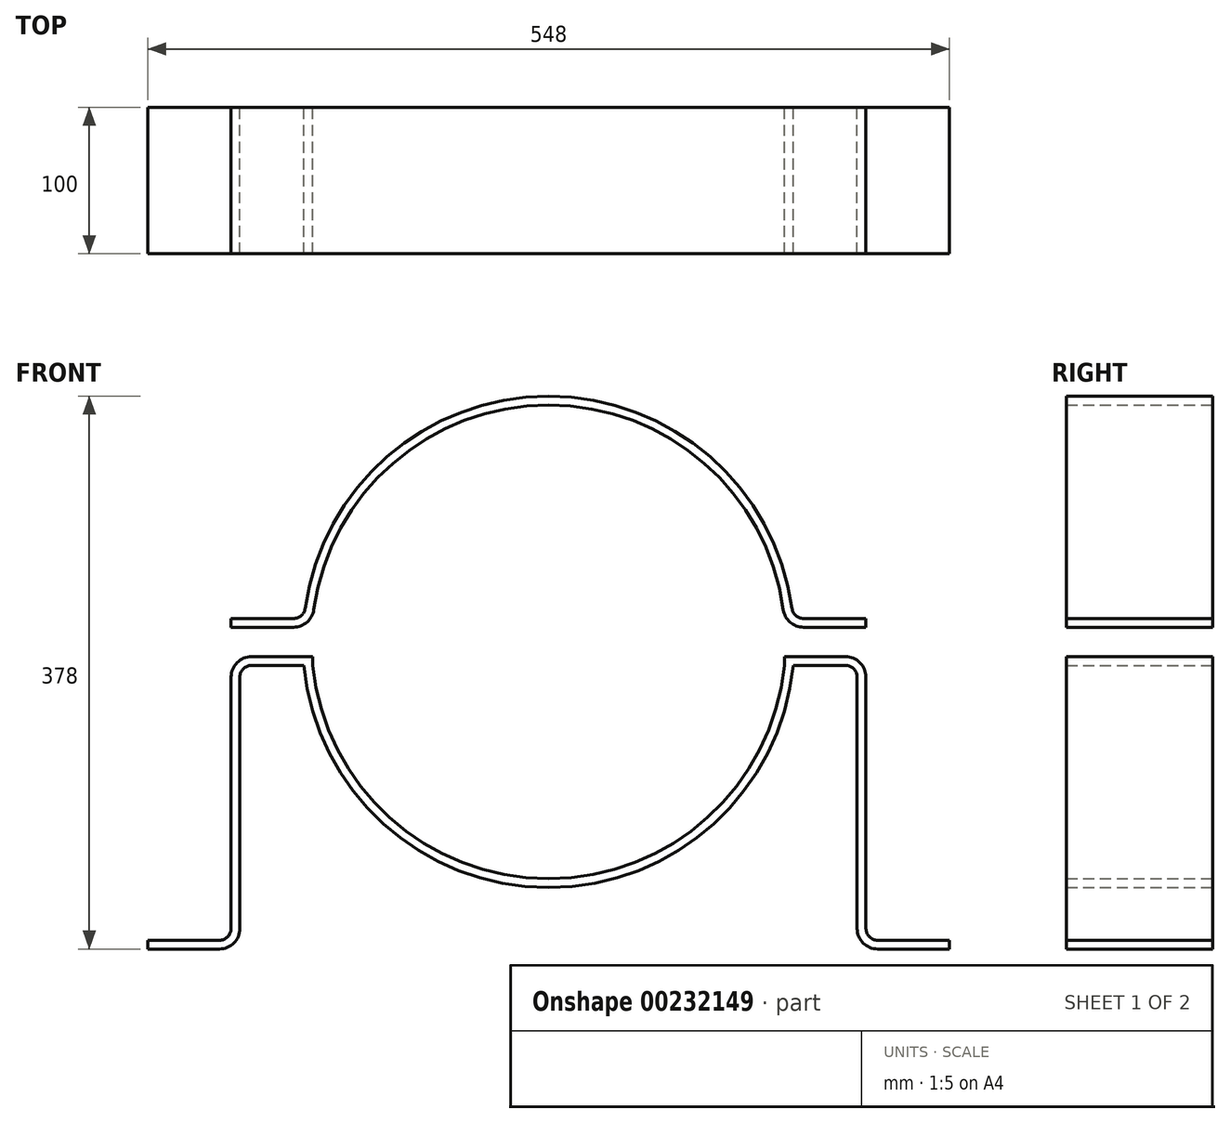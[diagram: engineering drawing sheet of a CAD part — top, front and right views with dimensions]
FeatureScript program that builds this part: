
annotation { "Feature Type Name" : "Feature", "Feature Type Description" : "" }
export const myFeature = defineFeature(function(context is Context, id is Id, definition is map)
    precondition{}
    {
        {
            var Q0;
            Q0=qCreatedBy(makeId("Front.planeOp"),FACE);
            var sketch = newSketch(context, id + "F0", { "sketchPlane" : qUnion([Q0])});
            skArc(sketch, "E0", {"start": v(160.49, 22.1) * mm, "mid": v(0, 162) * mm, "end": v(-160.49, 22.1) * mm});
            skArc(sketch, "E1.0", {"start": v(166.43, 22.9) * mm, "mid": v(0, 168) * mm, "end": v(-166.43, 22.9) * mm});
            skLineSegment(sketch, "E2", {"start": v(-168, 0) * mm, "end": v(168, 0) * mm, "construction": true});
            skLineSegment(sketch, "E3.0", {"start": v(-203, -10) * mm, "end": v(-161.2, -10) * mm});
            skLineSegment(sketch, "E4.0", {"start": v(-217, 10) * mm, "end": v(-174.36, 10) * mm});
            skLineSegment(sketch, "E5.0", {"start": v(-217, 16) * mm, "end": v(-174.36, 16) * mm});
            skLineSegment(sketch, "E6.0", {"start": v(-203, -16) * mm, "end": v(-161.2, -16) * mm});
            skLineSegment(sketch, "E7", {"start": v(0, 0) * mm, "end": v(0, -223.8) * mm, "construction": true});
            skLineSegment(sketch, "E8.0", {"start": v(-217, 16) * mm, "end": v(-217, 10) * mm});
            skLineSegment(sketch, "E9.0", {"start": v(217, 16) * mm, "end": v(217, 10) * mm});
            skPoint(sketch, "E10.orphan", {"position": v(-259.53, 0) * mm});
            skLineSegment(sketch, "E11.trimOffspring", {"start": v(-217, -24) * mm, "end": v(-217, -196) * mm});
            skLineSegment(sketch, "E12.trimOffspring", {"start": v(217, -24) * mm, "end": v(217, -196) * mm});
            skLineSegment(sketch, "E13", {"start": v(-225, -210) * mm, "end": v(-274, -210) * mm});
            skLineSegment(sketch, "E14", {"start": v(225, -210) * mm, "end": v(274, -210) * mm});
            skLineSegment(sketch, "E15.0", {"start": v(-225, -204) * mm, "end": v(-274, -204) * mm});
            skLineSegment(sketch, "E16.0", {"start": v(225, -204) * mm, "end": v(274, -204) * mm});
            skLineSegment(sketch, "E17.0", {"start": v(211, -24) * mm, "end": v(211, -196) * mm});
            skLineSegment(sketch, "E18.0", {"start": v(-211, -24) * mm, "end": v(-211, -196) * mm});
            skLineSegment(sketch, "E19", {"start": v(-274, -204) * mm, "end": v(-274, -210) * mm});
            skLineSegment(sketch, "E20", {"start": v(274, -210) * mm, "end": v(274, -204) * mm});
            skPoint(sketch, "E21.visualSharp", {"position": v(-217, -204) * mm});
            skArc(sketch, "E21.filletArc", {"start": v(-225, -204) * mm, "mid": v(-219.34, -201.66) * mm, "end": v(-217, -196) * mm});
            skPoint(sketch, "E22.visualSharp", {"position": v(217, -204) * mm});
            skArc(sketch, "E22.filletArc", {"start": v(217, -196) * mm, "mid": v(219.34, -201.66) * mm, "end": v(225, -204) * mm});
            skArc(sketch, "E23.filletArc", {"start": v(211, -24) * mm, "mid": v(208.66, -18.34) * mm, "end": v(203, -16) * mm});
            skArc(sketch, "E24.filletArc", {"start": v(-203, -16) * mm, "mid": v(-208.66, -18.34) * mm, "end": v(-211, -24) * mm});
            skPoint(sketch, "E25.visualSharp", {"position": v(-217, -10) * mm});
            skArc(sketch, "E25.filletArc", {"start": v(-203, -10) * mm, "mid": v(-212.9, -14.1) * mm, "end": v(-217, -24) * mm});
            skPoint(sketch, "E26.visualSharp", {"position": v(217, -10) * mm});
            skArc(sketch, "E26.filletArc", {"start": v(217, -24) * mm, "mid": v(212.9, -14.1) * mm, "end": v(203, -10) * mm});
            skPoint(sketch, "E27.visualSharp", {"position": v(-211, -210) * mm});
            skArc(sketch, "E27.filletArc", {"start": v(-225, -210) * mm, "mid": v(-215.1, -205.9) * mm, "end": v(-211, -196) * mm});
            skPoint(sketch, "E28.visualSharp", {"position": v(211, -210) * mm});
            skArc(sketch, "E28.filletArc", {"start": v(211, -196) * mm, "mid": v(215.1, -205.9) * mm, "end": v(225, -210) * mm});
            skArc(sketch, "E29.trimOffspring", {"start": v(-167.24, -16) * mm, "mid": v(0, -168) * mm, "end": v(167.24, -16) * mm});
            skArc(sketch, "E30.trimOffspring", {"start": v(-161.2, -16) * mm, "mid": v(0, -162) * mm, "end": v(161.2, -16) * mm});
            skLineSegment(sketch, "E31.trimOffspring", {"start": v(174.36, 16) * mm, "end": v(217, 16) * mm});
            skLineSegment(sketch, "E32.trimOffspring", {"start": v(174.36, 10) * mm, "end": v(217, 10) * mm});
            skPoint(sketch, "E33.visualSharp", {"position": v(-161.7, 10) * mm});
            skArc(sketch, "E33.filletArc", {"start": v(-174.36, 10) * mm, "mid": v(-165.16, 13.45) * mm, "end": v(-160.49, 22.1) * mm});
            skPoint(sketch, "E34.visualSharp", {"position": v(161.7, 10) * mm});
            skArc(sketch, "E34.filletArc", {"start": v(160.49, 22.1) * mm, "mid": v(165.16, 13.45) * mm, "end": v(174.36, 10) * mm});
            skPoint(sketch, "E35.visualSharp", {"position": v(167.24, 16) * mm});
            skArc(sketch, "E35.filletArc", {"start": v(166.43, 22.9) * mm, "mid": v(169.1, 17.97) * mm, "end": v(174.36, 16) * mm});
            skPoint(sketch, "E36.visualSharp", {"position": v(-167.24, 16) * mm});
            skArc(sketch, "E36.filletArc", {"start": v(-174.36, 16) * mm, "mid": v(-169.1, 17.97) * mm, "end": v(-166.43, 22.9) * mm});
            skLineSegment(sketch, "E37", {"start": v(-161.2, -16) * mm, "end": v(-161.2, -10) * mm});
            skLineSegment(sketch, "E38", {"start": v(161.2, -16) * mm, "end": v(161.2, -10) * mm});
            skLineSegment(sketch, "E39.trimOffspring", {"start": v(161.2, -10) * mm, "end": v(203, -10) * mm});
            skLineSegment(sketch, "E40.trimOffspring", {"start": v(161.2, -16) * mm, "end": v(203, -16) * mm});
            skSolve(sketch);
        }
        {
            var Q0;
            Q0 = qSketchRegion(id + "F0", true);
            extrude(context, id + "F1", {"entities" : qUnion([Q0]), "depth" : 100 * mm});
        }
    });
